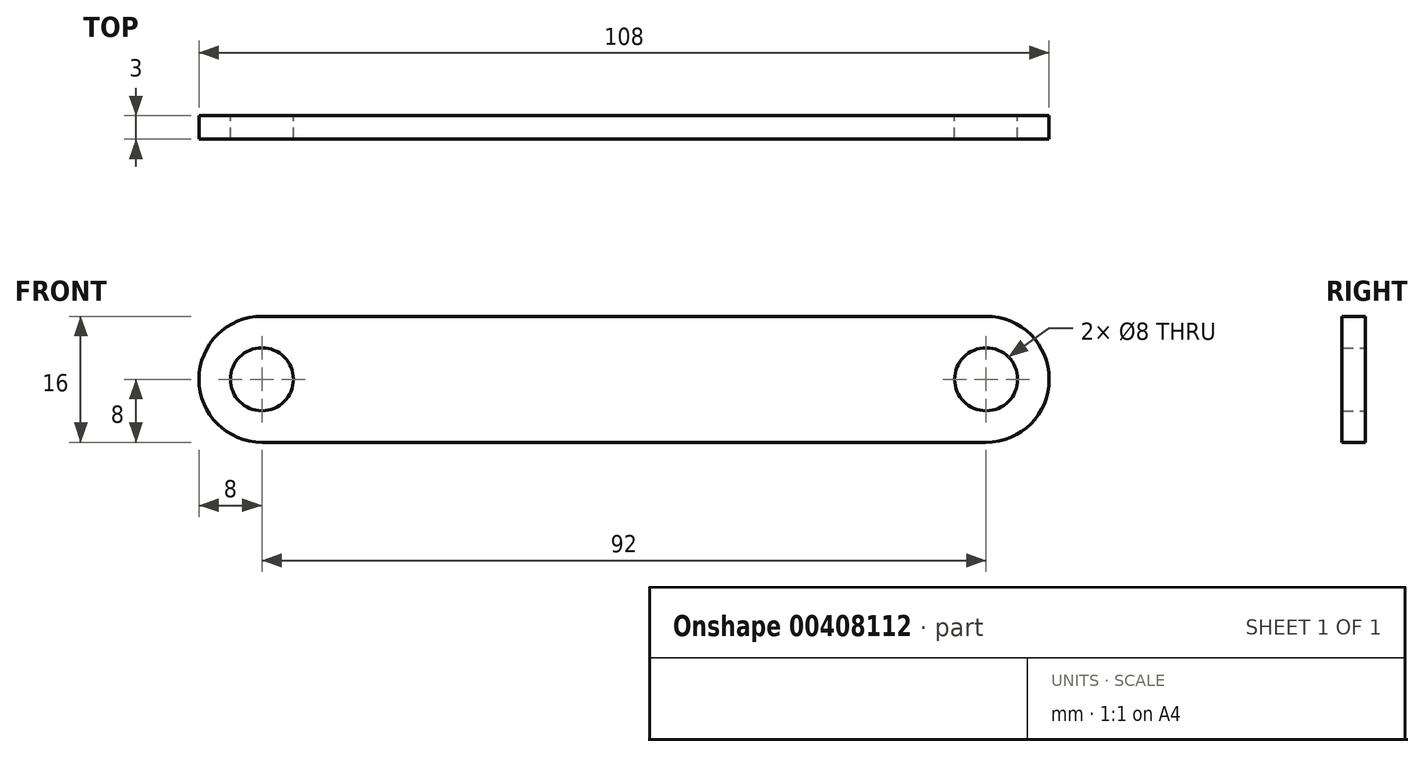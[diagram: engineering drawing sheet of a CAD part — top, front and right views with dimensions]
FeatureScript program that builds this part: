
annotation { "Feature Type Name" : "Feature", "Feature Type Description" : "" }
export const myFeature = defineFeature(function(context is Context, id is Id, definition is map)
    precondition{}
    {
        {
            var Q0;
            Q0=qCreatedBy(makeId("Front.planeOp"),FACE);
            var sketch = newSketch(context, id + "F0", { "sketchPlane" : qUnion([Q0])});
            skArc(sketch, "E0", {"start": v(-46, 8) * mm, "mid": v(-54, 0) * mm, "end": v(-46, -8) * mm});
            skArc(sketch, "E1", {"start": v(46, -8) * mm, "mid": v(54, 0) * mm, "end": v(46, 8) * mm});
            skLineSegment(sketch, "E2", {"start": v(-46, 8) * mm, "end": v(46, 8) * mm});
            skLineSegment(sketch, "E3", {"start": v(-46, -8) * mm, "end": v(46, -8) * mm});
            skCircle(sketch, "E4", {"center": v(-46, 0) * mm, "radius": 4 * mm});
            skCircle(sketch, "E5", {"center": v(46, 0) * mm, "radius": 4 * mm});
            skSolve(sketch);
        }
        {
            var Q0;
            Q0 = qSketchRegion(id + "F0", true);
            extrude(context, id + "F1", {"entities" : qUnion([Q0]), "endBound" : BoundingType.SYMMETRIC, "depth" : 3 * mm});
        }
    });
